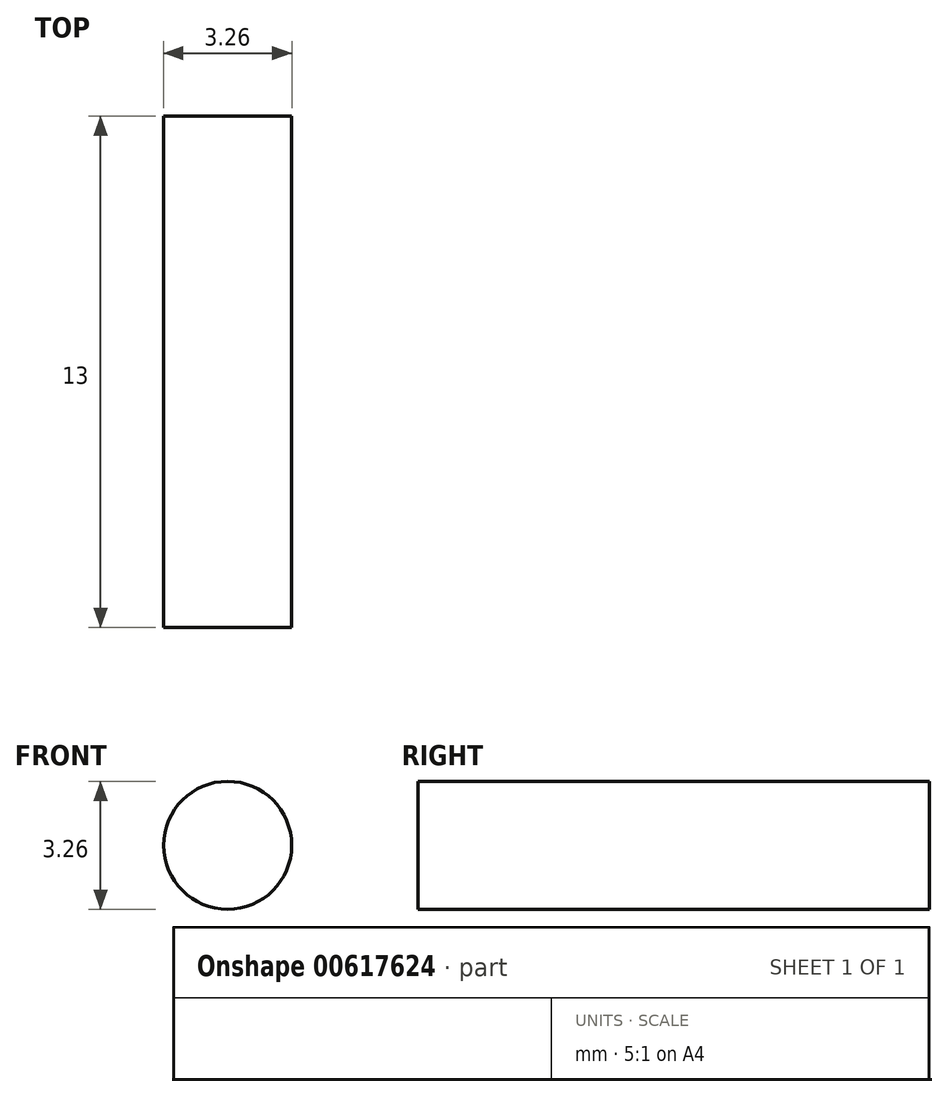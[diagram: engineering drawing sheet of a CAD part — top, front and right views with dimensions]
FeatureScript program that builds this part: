
annotation { "Feature Type Name" : "Feature", "Feature Type Description" : "" }
export const myFeature = defineFeature(function(context is Context, id is Id, definition is map)
    precondition{}
    {
        {
            var Q0;
            Q0=qCreatedBy(makeId("Front.planeOp"),FACE);
            var sketch = newSketch(context, id + "F0", { "sketchPlane" : qUnion([Q0])});
            skCircle(sketch, "E0", {"center": v(0, 0) * mm, "radius": 1.63 * mm});
            skSolve(sketch);
        }
        {
            var Q0;
            Q0=qSketchRegion(id+"F0",true);
            extrude(context, id + "F1", {"entities" : qUnion([Q0]), "depth" : 13 * mm, "offsetDistance" : 25 * mm});
        }
    });
